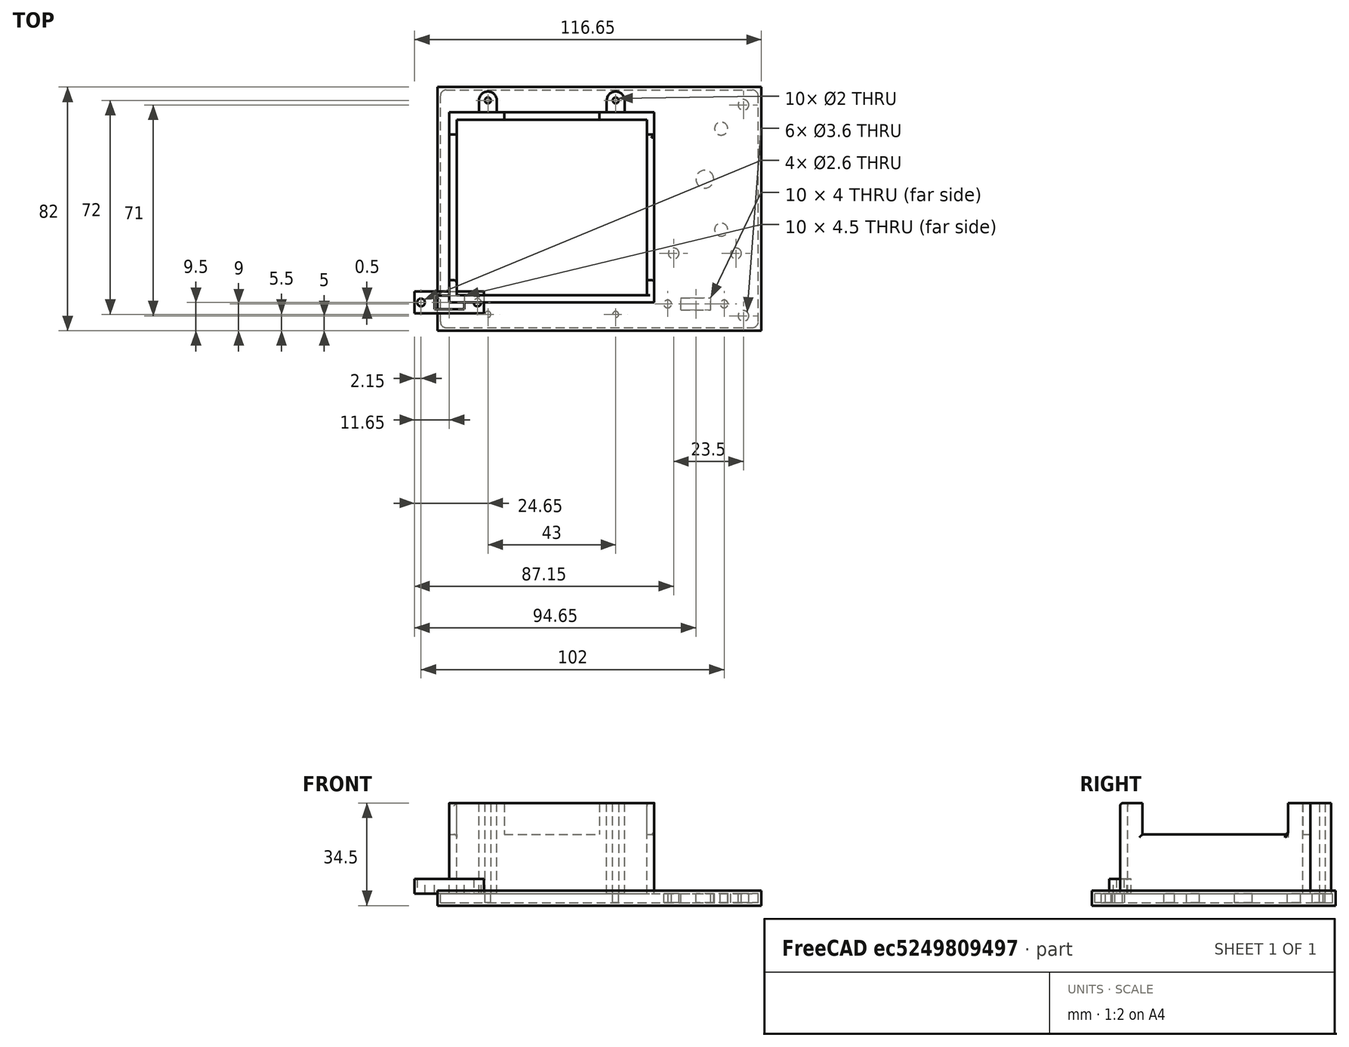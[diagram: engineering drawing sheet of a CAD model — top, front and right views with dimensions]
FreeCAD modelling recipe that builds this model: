
FCSTD DOCUMENT  (FreeCAD 0.19R)
Label: battery-5v
License: All rights reserved
LicenseURL: http://en.wikipedia.org/wiki/All_rights_reserved
objects: Part::FeaturePython×10, PartDesign::Body×7, App::Part×7, Part::Box×6, PartDesign::FeatureBase×6, Part::Cylinder×6, Path::FeaturePython×6, App::DocumentObjectGroup×4, Part::MultiFuse×3, Part::Cut×3, Sketcher::SketchObject×2, PartDesign::Pad×2, Part::Fillet×2, Mesh::Feature×2, App::FeaturePython×2, Path::FeatureCompoundPython×2, Spreadsheet::Sheet×1
note: 49 computed .brp shape members not serialized (recipe doc carries the construction recipe); baked Part::Feature solids carry a one-line shape summary decoded from their .brp

FEATURE [Part::Box] Box  label="Cube"
  AttacherType = Attacher::AttachEngine3D
  Height = 30.5
  Length = 64
  Placement = pos=(2.5,2.5,0) rot=(0,0,1;0rad)
  Width = 59
  expr: Length = <<p>>.int_sz_x
  expr: Width = <<p>>.int_sz_y
  expr: Height = <<p>>.height
  expr: .Placement.Base.x = <<p>>.wall
  expr: .Placement.Base.y = <<p>>.wall
FEATURE [Part::Box] Box001  label="Cube001"
  AttacherType = Attacher::AttachEngine3D
  Height = 30.5
  Length = 69
  Width = 64
  expr: Height = <<p>>.height
  expr: Width = <<p>>.int_sz_y + 2 * <<p>>.wall
  expr: Length = <<p>>.int_sz_x + 2 * <<p>>.wall
FEATURE [Sketcher::SketchObject] Sketch
  FullyConstrained = false
  MapMode = 5
  sketch-geometry (5):
    g0: LineSegment StartX=10 StartY=0 StartZ=0 EndX=10 EndY=-4 EndZ=0
    g1: LineSegment StartX=10 StartY=0 StartZ=0 EndX=16 EndY=0 EndZ=0
    g2: LineSegment StartX=16 StartY=0 StartZ=0 EndX=16 EndY=-4 EndZ=0
    g3: ArcOfCircle CenterX=13 CenterY=-4 CenterZ=0 NormalX=0 NormalY=0 NormalZ=1 AngleXU=0 Radius=3 StartAngle=3.14159 EndAngle=6.28319
    g4: Circle CenterX=13 CenterY=-4 CenterZ=0 NormalX=0 NormalY=0 NormalZ=1 AngleXU=0 Radius=1
  constraints (13):
    c: PointOnObject(g0,g-1)
    c: Vertical(g0)
    c: Coincident(g1,g0)
    c: Horizontal(g1)
    c: Coincident(g2,g1)
    c: Tangent(g3,g0) = -1.5708
    c: DistanceX(g1,g1) = 6
    c: Vertical(g2)
    c: Tangent(g2,g3) = 1.5708
    c: DistanceY(g0,g0) = 4
    c: DistanceX(g-1,g0) = 10
    c: Coincident(g4,g3)
    c: Radius(g4) = 1
FEATURE [PartDesign::Pad] Pad
  AllowMultiFace = false
  Direction = (1,1,1)
  Length = 30.5
  Length2 = 100
  Profile = -> Sketch
  Type = 0
  expr: Length = <<p>>.height
FEATURE [Spreadsheet::Sheet] Spreadsheet  label="p"
  cells = A1=height; B1(height)=30.5; A2=int_sz_x; B2(int_sz_x)=64; A3=int_sz_y; B3(int_sz_y)=59; A4=wall; B4(wall)=2.5; A5=plastic_sz_z; B5(plastic_sz_z)=3; A6=plastic_sz_x; B6(plastic_sz_x)=107; A7=plastic_sz_y; B7(plastic_sz_y)=80
FEATURE [Part::FeaturePython] Array  # Draft array (typed FeaturePython)
  Angle = 360
  ArrayType = 0
  Axis = (0,0,1)
  Base = -> Pad
  Center = (0,0,0)
  Fuse = false
  IntervalAxis = (0,0,0)
  IntervalX = (43,0,0)
  IntervalY = (0,1,0)
  IntervalZ = (0,0,1)
  NumberPolar = 1
  NumberX = 2
  NumberY = 1
  NumberZ = 1
  expr: .IntervalX.x = <<p>>.int_sz_x + 2 * <<p>>.wall - 20 - 6
FEATURE [PartDesign::FeatureBase] Clone
  BaseFeature = -> Array
FEATURE [PartDesign::Body] Body  label="attach clone"
  BaseFeature = -> Array
  Group = -> [Clone]
  Origin = -> Origin004
  Placement = pos=(69,64,0) rot=(0,0,1;3.14159rad)
  Tip = -> Clone
FEATURE [App::Part] Part001  label="attach"
  Group = -> [Sketch,Pad,Array,Body]
  Origin = -> Origin003
FEATURE [Part::Box] Box002  label="cut cube"
  AttacherType = Attacher::AttachEngine3D
  Height = 12
  Length = 200
  Placement = pos=(-50,7.5,20) rot=(0,0,1;0rad)
  Width = 49
  expr: Width = <<p>>.int_sz_y - 10
  expr: .Placement.Base.y = <<p>>.wall + 5
FEATURE [Part::Box] Box003  label="cut cube001"
  AttacherType = Attacher::AttachEngine3D
  Height = 12
  Length = 32
  Placement = pos=(18.5,7.5,20) rot=(0,0,1;0rad)
  Width = 200
  expr: .Placement.Base.y = <<p>>.wall + 5
  expr: Length = <<p>>.int_sz_x - 32
FEATURE [Part::MultiFuse] Fusion
  Shapes = -> [Box,Box002,Box003]
FEATURE [Part::Cut] Cut
  Base = -> Box001
  Tool = -> Fusion
FEATURE [Part::Fillet] Fillet
  Base = -> Cut
  Edges = 9 edges r=1: [Edge9,Edge12,Edge15,Edge16,Edge19,Edge21,Edge48,Edge49,Edge60]
FEATURE [App::Part] Part
  Group = -> [Box,Box001,Cut,Box003,Fusion,Box002,Fillet]
  Origin = -> Origin
FEATURE [Part::Box] Box004  label="plane"
  AttacherType = Attacher::AttachEngine3D
  Height = 3
  Length = 107
  Placement = pos=(-3,-8.5,-3) rot=(0,0,1;0rad)
  Width = 80
  expr: Height = <<p>>.plastic_sz_z
  expr: Length = <<p>>.plastic_sz_x
  expr: Width = <<p>>.plastic_sz_y
FEATURE [Mesh::Feature] step_down_12_1_8v  label="step_down_12-1.8v"
  Placement = pos=(79.5,5,0) rot=(0,0,1;0rad)
FEATURE [Sketcher::SketchObject] Sketch001
  FullyConstrained = false
  MapMode = 5
  Support = -> [XY_Plane007]
  sketch-geometry (10):
    g0: LineSegment StartX=-11.65 StartY=3.7 StartZ=0 EndX=11.65 EndY=3.7 EndZ=0
    g1: LineSegment StartX=11.65 StartY=3.7 StartZ=0 EndX=11.65 EndY=-3.7 EndZ=0
    g2: LineSegment StartX=11.65 StartY=-3.7 StartZ=0 EndX=-11.65 EndY=-3.7 EndZ=0
    g3: LineSegment StartX=-11.65 StartY=-3.7 StartZ=0 EndX=-11.65 EndY=3.7 EndZ=0
    g4: LineSegment StartX=-5 StartY=2.25 StartZ=0 EndX=5 EndY=2.25 EndZ=0
    g5: LineSegment StartX=5 StartY=2.25 StartZ=0 EndX=5 EndY=-2.25 EndZ=0
    g6: LineSegment StartX=5 StartY=-2.25 StartZ=0 EndX=-5 EndY=-2.25 EndZ=0
    g7: LineSegment StartX=-5 StartY=-2.25 StartZ=0 EndX=-5 EndY=2.25 EndZ=0
    g8: Circle CenterX=-9.5 CenterY=0 CenterZ=0 NormalX=0 NormalY=0 NormalZ=1 AngleXU=0 Radius=1.3
    g9: Circle CenterX=9.5 CenterY=0 CenterZ=0 NormalX=0 NormalY=0 NormalZ=1 AngleXU=0 Radius=1.3
  constraints (25):
    c: Coincident(g0,g1)
    c: Coincident(g1,g2)
    c: Coincident(g2,g3)
    c: Coincident(g3,g0)
    c: Horizontal(g0)
    c: Vertical(g1)
    c: Coincident(g4,g5)
    c: Coincident(g5,g6)
    c: Coincident(g6,g7)
    c: Coincident(g7,g4)
    c: Horizontal(g4)
    c: Vertical(g5)
    c: Symmetric(g4,g6,g-1)
    c: Symmetric(g0,g2,g-1)
    c: DistanceY(g5,g5) = 4.5
    c: DistanceY(g1,g1) = 7.4
    c: DistanceX(g8,g9) = 19
    c: DistanceX(g0,g0) = 23.3
    c: Symmetric(g2,g1,g-2)
    c: Symmetric(g6,g5,g-2)
    c: DistanceX(g6,g6) = 10
    c: Symmetric(g8,g9,g-2)
    c: DistanceY(g8,g-1) = 0
    c: Radius(g8) = 1.3
    c: Equal(g8,g9)
FEATURE [PartDesign::Pad] Pad001
  AllowMultiFace = false
  Direction = (1,1,1)
  Length = 5
  Length2 = 100
  Profile = -> Sketch001
  Type = 0
FEATURE [PartDesign::Body] Body001
  Group = -> [Sketch001,Pad001]
  Origin = -> Origin007
  Tip = -> Pad001
FEATURE [App::Part] Part003  label="switch mockup plane"
  Group = -> [Body001]
  Origin = -> Origin006
  Placement = pos=(83,-0.5,0) rot=(0,0,1;0rad)
FEATURE [Part::Cylinder] Cylinder
  Angle = 360
  AttacherType = Attacher::AttachEngine3D
  Height = 40
  Placement = pos=(73.5,-0.5,-15) rot=(0,0,-1;1.5708rad)
  Radius = 1.3
FEATURE [Part::FeaturePython] Array001  # Draft array (typed FeaturePython)
  Angle = 360
  ArrayType = 0
  Axis = (0,0,1)
  Base = -> Cylinder
  Center = (0,0,0)
  Fuse = false
  IntervalAxis = (0,0,0)
  IntervalX = (19,0,0)
  IntervalY = (0,19,0)
  IntervalZ = (0,0,1)
  NumberPolar = 1
  NumberX = 2
  NumberY = 1
  NumberZ = 1
FEATURE [Part::Cylinder] Cylinder001
  Angle = 360
  AttacherType = Attacher::AttachEngine3D
  Height = 40
  Placement = pos=(75.5,16.5,-15) rot=(0,0,1;0rad)
  Radius = 1.8
FEATURE [Part::FeaturePython] Array002  # Draft array (typed FeaturePython)
  Angle = 360
  ArrayType = 0
  Axis = (0,0,1)
  Base = -> Cylinder001
  Center = (0,0,0)
  Fuse = false
  IntervalAxis = (0,0,0)
  IntervalX = (21,0,0)
  IntervalY = (0,1,0)
  IntervalZ = (0,0,1)
  NumberPolar = 1
  NumberX = 2
  NumberY = 1
  NumberZ = 1
FEATURE [Part::Cylinder] Cylinder002
  Angle = 360
  AttacherType = Attacher::AttachEngine3D
  Height = 100
  Placement = pos=(13,-4,-15) rot=(0,0,1;0rad)
  Radius = 1
FEATURE [Part::FeaturePython] Array003  label="Array battery holder holes"  # Draft array (typed FeaturePython)
  Angle = 360
  ArrayType = 0
  Axis = (0,0,1)
  Base = -> Cylinder002
  Center = (0,0,0)
  Fuse = false
  IntervalAxis = (0,0,0)
  IntervalX = (43,0,0)
  IntervalY = (0,72,0)
  IntervalZ = (0,0,1)
  NumberPolar = 1
  NumberX = 2
  NumberY = 2
  NumberZ = 1
FEATURE [Part::Cylinder] Cylinder003
  Angle = 360
  AttacherType = Attacher::AttachEngine3D
  Height = 40
  Placement = pos=(99,-4.5,-15) rot=(0,0,1;0rad)
  Radius = 1.8
FEATURE [Part::FeaturePython] Array004  label="Array corners"  # Draft array (typed FeaturePython)
  Angle = 360
  ArrayType = 0
  Axis = (0,0,1)
  Base = -> Cylinder003
  Center = (0,0,0)
  Fuse = false
  IntervalAxis = (0,0,0)
  IntervalX = (1,0,0)
  IntervalY = (0,71,0)
  IntervalZ = (0,0,1)
  NumberPolar = 1
  NumberX = 1
  NumberY = 2
  NumberZ = 1
FEATURE [Part::Box] Box005  label="Cube switch cut"
  AttacherType = Attacher::AttachEngine3D
  Height = 40
  Length = 4
  Placement = pos=(78,1.5,-10) rot=(0,0,-1;1.5708rad)
  Width = 10
FEATURE [Mesh::Feature] usb_female_case_v2
  Placement = pos=(103,53,-4.5) rot=(-0.707107,0.707107,0;3.14159rad)
FEATURE [Part::Cylinder] Cylinder004
  Angle = 360
  AttacherType = Attacher::AttachEngine3D
  Height = 40
  Placement = pos=(91.5,24.5,-15) rot=(0,0,1;0rad)
  Radius = 2.2
FEATURE [Part::FeaturePython] Array005  label="Array usb"  # Draft array (typed FeaturePython)
  Angle = 360
  ArrayType = 0
  Axis = (0,0,1)
  Base = -> Cylinder004
  Center = (0,0,0)
  Fuse = false
  IntervalAxis = (0,0,0)
  IntervalX = (1,0,0)
  IntervalY = (0,34,0)
  IntervalZ = (0,0,1)
  NumberPolar = 1
  NumberX = 1
  NumberY = 2
  NumberZ = 1
FEATURE [Part::Cylinder] Cylinder005  label="Cylinder usb center"
  Angle = 360
  AttacherType = Attacher::AttachEngine3D
  Height = 40
  Placement = pos=(86,41.5,-15) rot=(0,0,1;0rad)
  Radius = 3
FEATURE [Part::MultiFuse] Fusion001
  Shapes = -> [Array001,Array002,Array003,Array004,Box005,Array005,Cylinder005]
FEATURE [App::FeaturePython] SetupSheet  # Path/CAM operation (typed FeaturePython)
  ClearanceHeightExpression = OpStockZMax+SetupSheet.ClearanceHeightOffset
  ClearanceHeightOffset = 5
  CoolantMode = 0
  CoolantModes = None | Flood | Mist
  FinalDepthExpression = OpFinalDepth
  HorizRapid = 100
  SafeHeightExpression = OpStockZMax+SetupSheet.SafeHeightOffset
  SafeHeightOffset = 3
  StartDepthExpression = OpStartDepth
  StepDownExpression = OpToolDiameter
  VertRapid = 100
FEATURE [Path::FeaturePython] T3__laser  label="T3: laser"  # Path/CAM operation (typed FeaturePython)
  HorizFeed = 1
  HorizRapid = 100
  SpindleDir = 0
  SpindleSpeed = 0
  ToolNumber = 3
  VertFeed = 1
  VertRapid = 100
  expr: VertRapid = SetupSheet.VertRapid
  expr: HorizRapid = SetupSheet.HorizRapid
FEATURE [Part::Fillet] Fillet001
  Base = -> Box004
  Edges = 4 edges r=2: [Edge1,Edge3,Edge5,Edge7]
FEATURE [Part::Cut] Cut001
  Base = -> Fillet001
  Tool = -> Fusion001
FEATURE [App::Part] Part002  label="top plane part"
  Group = -> [Box004,Cylinder,Array001,Cylinder001,Array002,Cylinder002,Array003,Fusion001,Cut001,Cylinder003,Array004,Box005,Cylinder004,Array005,Cylinder005,Fillet001]
  Origin = -> Origin005
FEATURE [PartDesign::FeatureBase] Clone002
  BaseFeature = -> Cut001
FEATURE [PartDesign::Body] Body002  label="top lid clone"
  BaseFeature = -> Cut001
  Group = -> [Clone002]
  Origin = -> Origin008
  Tip = -> Clone002
FEATURE [App::Part] Part004  label="top lid clone for job"
  Group = -> [Body002]
  Origin = -> Origin009
FEATURE [Part::FeaturePython] Clone001  label="Model-top plane part"  # Draft clone (typed FeaturePython)
  AttacherType = Attacher::AttachEngine3D
  Fuse = false
  Objects = -> [Part004]
  PathResource = Model
  Scale = (1,1,1)
FEATURE [App::DocumentObjectGroup] Model
  Group = -> [Clone001]
FEATURE [Part::FeaturePython] Stock001  # WARN: FeaturePython — macro-defined, semantics opaque (R4)
  Base = -> Model
  ExtXneg = 1
  ExtXpos = 1
  ExtYneg = 1
  ExtYpos = 1
  ExtZneg = 1
  ExtZpos = 1
  Placement = pos=(-3,-8.5,-3) rot=(0,0,1;0rad)
  StockType = FromBase
FEATURE [Path::FeaturePython] Engrave  # Path/CAM operation (typed FeaturePython)
  Active = true
  Base = -> [Clone001]
  ClearanceHeight = 6
  FinalDepth = -0.2
  OpFinalDepth = -0.2
  OpStartDepth = 0
  OpStockZMax = 1
  OpStockZMin = -4
  OpToolDiameter = 0.2
  SafeHeight = 4
  StartDepth = 0
  StartVertex = 0
  StepDown = 0.2
  ToolController = -> T3__laser
  expr: StartDepth = OpStartDepth
  expr: FinalDepth = OpFinalDepth
  expr: StepDown = OpToolDiameter
  expr: SafeHeight = OpStockZMax + SetupSheet.SafeHeightOffset
  expr: ClearanceHeight = OpStockZMax + SetupSheet.ClearanceHeightOffset
FEATURE [Path::FeatureCompoundPython] Operations  # Path/CAM operation (typed FeaturePython)
  Group = -> [Engrave]
  UsePlacements = false
FEATURE [PartDesign::FeatureBase] Clone003
  BaseFeature = -> Fillet001
FEATURE [PartDesign::Body] Body003  label="Body plane clone"
  BaseFeature = -> Fillet001
  Group = -> [Clone003]
  Origin = -> Origin011
  Tip = -> Clone003
FEATURE [PartDesign::FeatureBase] Clone004
  BaseFeature = -> Array003
FEATURE [PartDesign::Body] Body004  label="Body battery holes clone"
  BaseFeature = -> Array003
  Group = -> [Clone004]
  Origin = -> Origin012
  Tip = -> Clone004
FEATURE [PartDesign::FeatureBase] Clone005
  BaseFeature = -> Array004
FEATURE [PartDesign::Body] Body005  label="Body corners"
  BaseFeature = -> Array004
  Group = -> [Clone005]
  Origin = -> Origin013
  Tip = -> Clone005
FEATURE [Part::MultiFuse] Fusion002
  Shapes = -> [Body004,Body005]
FEATURE [Part::Cut] Cut002
  Base = -> Body003
  Tool = -> Fusion002
FEATURE [App::Part] Part005  label="bottom plane part"
  Group = -> [Body003,Body004,Body005,Fusion002,Cut002]
  Origin = -> Origin010
FEATURE [PartDesign::FeatureBase] Clone006
  BaseFeature = -> Cut002
FEATURE [PartDesign::Body] Body006
  BaseFeature = -> Cut002
  Group = -> [Clone006]
  Origin = -> Origin014
  Tip = -> Clone006
FEATURE [App::Part] Part006  label="bottom plane part clone for job"
  Group = -> [Body006]
  Origin = -> Origin015
FEATURE [App::FeaturePython] SetupSheet001  # Path/CAM operation (typed FeaturePython)
  ClearanceHeightExpression = OpStockZMax+SetupSheet001.ClearanceHeightOffset
  ClearanceHeightOffset = 0
  CoolantMode = 0
  CoolantModes = None | Flood | Mist
  FinalDepthExpression = OpFinalDepth
  HorizRapid = 100
  SafeHeightExpression = OpStockZMax+SetupSheet001.SafeHeightOffset
  SafeHeightOffset = 0
  StartDepthExpression = OpStartDepth
  StepDownExpression = OpToolDiameter
  VertRapid = 100
FEATURE [Part::FeaturePython] Clone007  label="Model-bottom plane part clone for job"  # Draft clone (typed FeaturePython)
  AttacherType = Attacher::AttachEngine3D
  Fuse = false
  Objects = -> [Part006]
  PathResource = Model
  Scale = (1,1,1)
FEATURE [App::DocumentObjectGroup] Model001
  Group = -> [Clone007]
FEATURE [Part::FeaturePython] Stock  # WARN: FeaturePython — macro-defined, semantics opaque (R4)
  Base = -> Model001
  ExtXneg = 1
  ExtXpos = 1
  ExtYneg = 1
  ExtYpos = 1
  ExtZneg = 1
  ExtZpos = 1
  Placement = pos=(-3,-8.5,-3) rot=(0,0,1;0rad)
  StockType = FromBase
FEATURE [Path::FeaturePython] T3__laser001  label="T3: laser001"  # Path/CAM operation (typed FeaturePython)
  HorizFeed = 0.5
  HorizRapid = 100
  SpindleDir = 0
  SpindleSpeed = 1000
  ToolNumber = 3
  VertFeed = 0.5
  VertRapid = 100
  expr: VertRapid = SetupSheet001.VertRapid
  expr: HorizRapid = SetupSheet001.HorizRapid
FEATURE [Path::FeaturePython] Engrave001  # Path/CAM operation (typed FeaturePython)
  Active = true
  Base = -> [Clone007]
  ClearanceHeight = 1
  FinalDepth = 0
  OpFinalDepth = -0.2
  OpStartDepth = 0
  OpStockZMax = 1
  OpStockZMin = -4
  OpToolDiameter = 0.2
  SafeHeight = 1
  StartDepth = 0
  StartVertex = 0
  StepDown = 0.2
  ToolController = -> T3__laser001
  expr: StartDepth = OpStartDepth
  expr: StepDown = OpToolDiameter
  expr: SafeHeight = OpStockZMax + SetupSheet001.SafeHeightOffset
  expr: ClearanceHeight = OpStockZMax + SetupSheet001.ClearanceHeightOffset
FEATURE [Path::FeatureCompoundPython] Operations001  # Path/CAM operation (typed FeaturePython)
  Group = -> [Engrave001]
  UsePlacements = false
FEATURE [App::DocumentObjectGroup] Tools
  Group = -> [T3__laser]
FEATURE [Path::FeaturePython] Job  label="top lid job"  # Path/CAM operation (typed FeaturePython)
  CycleTime = 00:00:00
  GeometryTolerance = 0.01
  Model = -> Model
  Operations = -> Operations
  PostProcessor = 1
  PostProcessorOutputFile = <userpath>/work/roborep/gcode
  SetupSheet = -> SetupSheet
  Stock = -> Stock001
  Tools = -> Tools
FEATURE [App::DocumentObjectGroup] Tools001  label="Tools"
  Group = -> [T3__laser001]
FEATURE [Path::FeaturePython] Job001  label="bottom plane job"  # Path/CAM operation (typed FeaturePython)
  CycleTime = 00:00:00
  GeometryTolerance = 0.01
  Model = -> Model001
  Operations = -> Operations001
  PostProcessor = 1
  PostProcessorOutputFile = <userpath>/work/roborep/freecad/battery-5v/bottom_plate.gcode
  SetupSheet = -> SetupSheet001
  Stock = -> Stock
  Tools = -> Tools001
